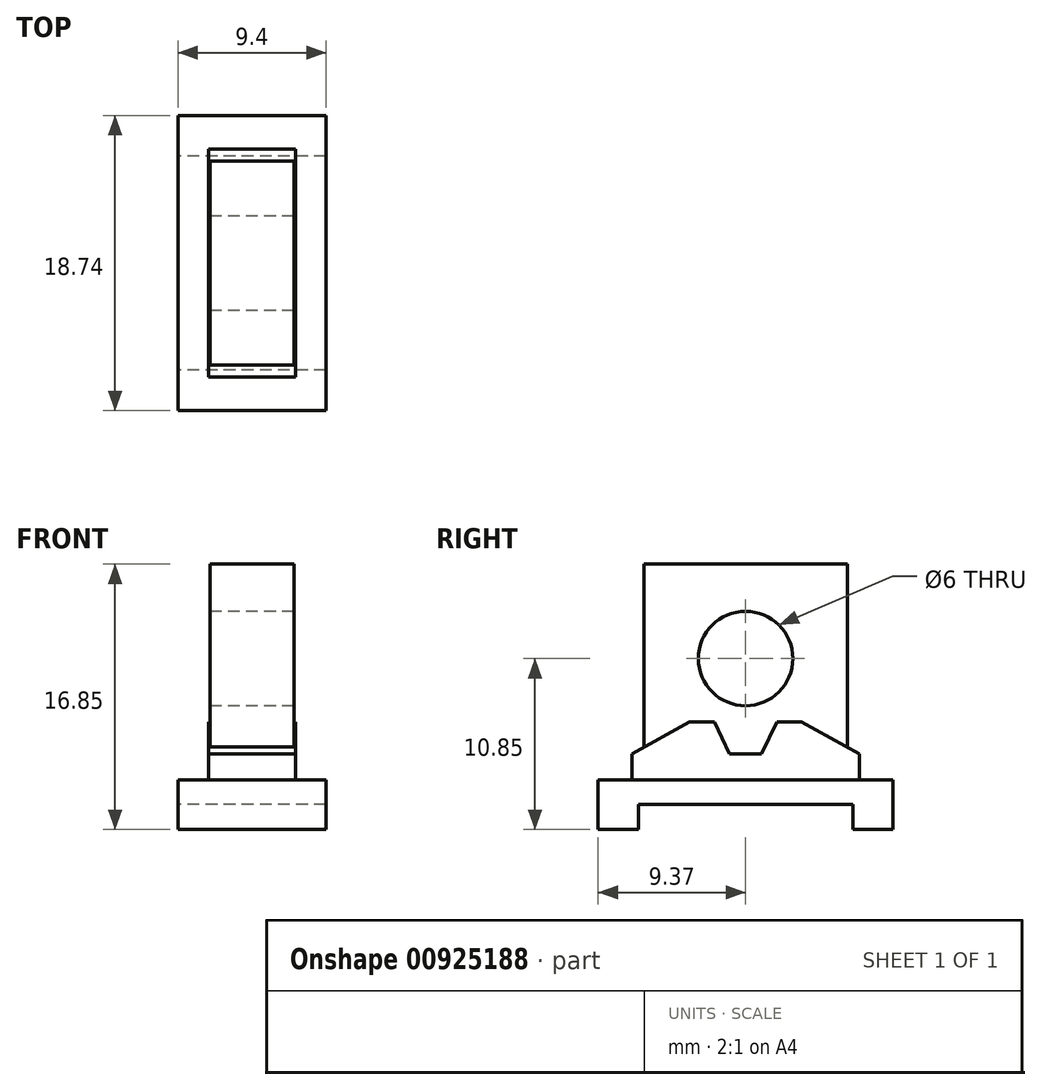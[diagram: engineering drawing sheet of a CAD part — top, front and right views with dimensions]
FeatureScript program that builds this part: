
annotation { "Feature Type Name" : "Feature", "Feature Type Description" : "" }
export const myFeature = defineFeature(function(context is Context, id is Id, definition is map)
    precondition{}
    {
        {
            var Q0;
            Q0=qCreatedBy(makeId("Right.planeOp"),FACE);
            var sketch = newSketch(context, id + "F0", { "sketchPlane" : qUnion([Q0])});
            skLineSegment(sketch, "E0.bottom", {"start": v(-9.37, 3.15) * mm, "end": v(9.37, 3.15) * mm});
            skLineSegment(sketch, "E0.left", {"start": v(-9.37, 3.15) * mm, "end": v(-9.37, 0) * mm});
            skLineSegment(sketch, "E0.right", {"start": v(9.37, 3.15) * mm, "end": v(9.37, 0) * mm});
            skLineSegment(sketch, "E1.bottom", {"start": v(-6.8, 0) * mm, "end": v(6.8, 0) * mm, "construction": true});
            skLineSegment(sketch, "E1.top", {"start": v(-6.8, 1.57) * mm, "end": v(6.8, 1.57) * mm});
            skLineSegment(sketch, "E1.left", {"start": v(-6.8, 0) * mm, "end": v(-6.8, 1.57) * mm});
            skLineSegment(sketch, "E1.right", {"start": v(6.8, 0) * mm, "end": v(6.8, 1.57) * mm});
            skLineSegment(sketch, "E2", {"start": v(-9.37, 0) * mm, "end": v(-6.8, 0) * mm});
            skLineSegment(sketch, "E3", {"start": v(6.8, 0) * mm, "end": v(9.37, 0) * mm});
            skSolve(sketch);
        }
        {
            var Q0;
            Q0 = qSketchRegion(id + "F0", true);
            extrude(context, id + "F1", {"entities" : qUnion([Q0]), "endBound" : BoundingType.SYMMETRIC, "depth" : 9.4 * mm, "offsetDistance" : 25.4 * mm});
        }
        {
            var Q0;
            Q0=qCreatedBy(makeId("Right.planeOp"),FACE);
            var sketch = newSketch(context, id + "F2", { "sketchPlane" : qUnion([Q0])});
            skLineSegment(sketch, "E4.bottom", {"start": v(-7.23, 4.8) * mm, "end": v(7.23, 4.8) * mm, "construction": true});
            skLineSegment(sketch, "E4.top", {"start": v(-7.23, 3.15) * mm, "end": v(7.23, 3.15) * mm});
            skLineSegment(sketch, "E4.left", {"start": v(-7.23, 4.8) * mm, "end": v(-7.23, 3.15) * mm});
            skLineSegment(sketch, "E4.right", {"start": v(7.23, 4.8) * mm, "end": v(7.23, 3.15) * mm});
            skLineSegment(sketch, "E5", {"start": v(0, 4.8) * mm, "end": v(0, 0) * mm, "construction": true});
            skLineSegment(sketch, "E6", {"start": v(-7.23, 4.8) * mm, "end": v(-3.56, 6.83) * mm});
            skLineSegment(sketch, "E7", {"start": v(-3.56, 6.83) * mm, "end": v(-2, 6.83) * mm});
            skLineSegment(sketch, "E8", {"start": v(-2, 6.83) * mm, "end": v(-1.02, 4.8) * mm});
            skLineSegment(sketch, "E9", {"start": v(-1.02, 4.8) * mm, "end": v(0, 4.8) * mm});
            skLineSegment(sketch, "E10.MirrorCS", {"start": v(2, 6.83) * mm, "end": v(1.02, 4.8) * mm});
            skLineSegment(sketch, "E11.MirrorCS", {"start": v(3.56, 6.83) * mm, "end": v(2, 6.83) * mm});
            skLineSegment(sketch, "E12.MirrorCS", {"start": v(7.23, 4.8) * mm, "end": v(3.56, 6.83) * mm});
            skLineSegment(sketch, "E13", {"start": v(0, 4.8) * mm, "end": v(1.02, 4.8) * mm});
            skSolve(sketch);
        }
        {
            var Q0;
            Q0 = qSketchRegion(id + "F2", true);
            extrude(context, id + "F3", {"entities" : qUnion([Q0]), "operationType" : NewBodyOperationType.ADD, "endBound" : BoundingType.SYMMETRIC, "depth" : 5.5 * mm, "offsetDistance" : 25.4 * mm});
        }
        {
            var Q0;
            Q0=qCreatedBy(makeId("Right.planeOp"),FACE);
            var sketch = newSketch(context, id + "F4", { "sketchPlane" : qUnion([Q0])});
            skLineSegment(sketch, "E14.bottom", {"start": v(-6.46, 3.15) * mm, "end": v(6.46, 3.15) * mm});
            skLineSegment(sketch, "E14.top", {"start": v(-6.46, 16.85) * mm, "end": v(6.46, 16.85) * mm});
            skLineSegment(sketch, "E14.left", {"start": v(-6.46, 3.15) * mm, "end": v(-6.46, 16.85) * mm});
            skLineSegment(sketch, "E14.right", {"start": v(6.46, 3.15) * mm, "end": v(6.46, 16.85) * mm});
            skLineSegment(sketch, "E15", {"start": v(0, 3.15) * mm, "end": v(0, 0) * mm, "construction": true});
            skCircle(sketch, "E16", {"center": v(0, 10.85) * mm, "radius": 3 * mm});
            skPoint(sketch, "E16.centerSnap0", {"position": v(0, 16.85) * mm});
            skSolve(sketch);
        }
        {
            var Q0;
            Q0 = qSketchRegion(id + "F4", true);
            extrude(context, id + "F5", {"entities" : qUnion([Q0]), "operationType" : NewBodyOperationType.ADD, "endBound" : BoundingType.SYMMETRIC, "depth" : 5.33 * mm, "offsetDistance" : 25.4 * mm});
        }
    });
